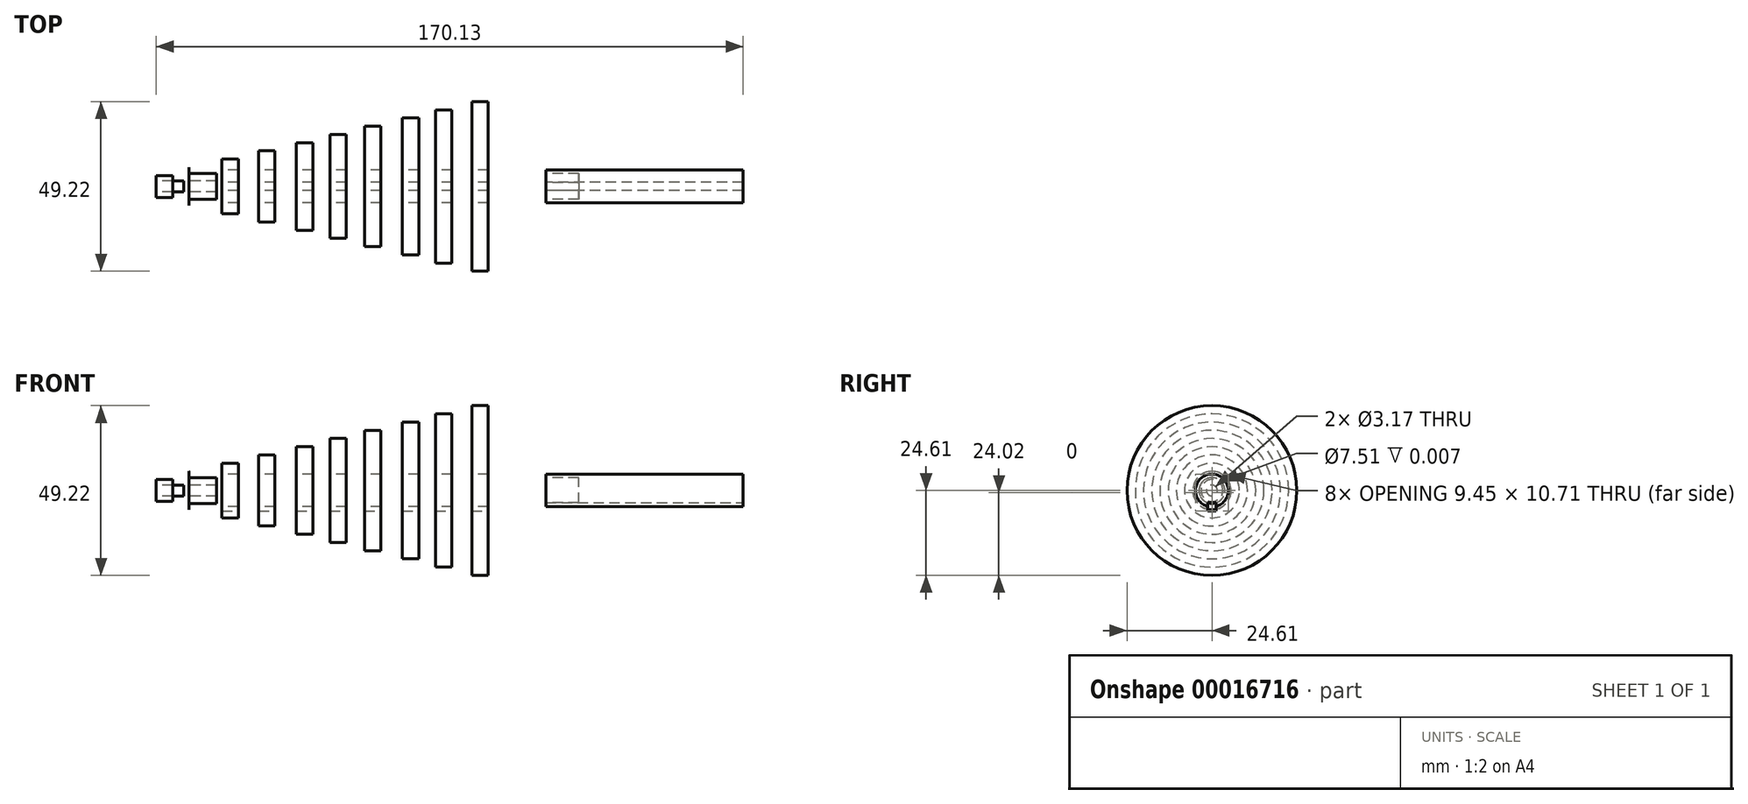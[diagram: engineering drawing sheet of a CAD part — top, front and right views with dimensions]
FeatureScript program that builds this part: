
annotation { "Feature Type Name" : "Feature", "Feature Type Description" : "" }
export const myFeature = defineFeature(function(context is Context, id is Id, definition is map)
    precondition{}
    {
        {
            var Q0;
            Q0=qCreatedBy(makeId("Front.planeOp"),FACE);
            var sketch = newSketch(context, id + "F0", { "sketchPlane" : qUnion([Q0])});
            skLineSegment(sketch, "E0.bottom", {"start": v(-46.34, 7.94) * mm, "end": v(-41.57, 7.94) * mm});
            skLineSegment(sketch, "E0.top", {"start": v(-46.34, 4.76) * mm, "end": v(-41.57, 4.76) * mm});
            skLineSegment(sketch, "E0.left", {"start": v(-46.34, 7.94) * mm, "end": v(-46.34, 4.76) * mm});
            skLineSegment(sketch, "E0.right", {"start": v(-41.57, 7.94) * mm, "end": v(-41.57, 4.76) * mm});
            skLineSegment(sketch, "E1.bottom", {"start": v(-35.72, 10.32) * mm, "end": v(-30.95, 10.32) * mm});
            skLineSegment(sketch, "E1.top", {"start": v(-35.72, 4.76) * mm, "end": v(-30.95, 4.76) * mm});
            skLineSegment(sketch, "E1.left", {"start": v(-35.72, 10.32) * mm, "end": v(-35.72, 4.76) * mm});
            skLineSegment(sketch, "E1.right", {"start": v(-30.95, 10.32) * mm, "end": v(-30.95, 4.76) * mm});
            skLineSegment(sketch, "E2.bottom", {"start": v(-24.77, 12.7) * mm, "end": v(-20.01, 12.7) * mm});
            skLineSegment(sketch, "E2.top", {"start": v(-24.77, 4.76) * mm, "end": v(-20.01, 4.76) * mm});
            skLineSegment(sketch, "E2.left", {"start": v(-24.77, 12.7) * mm, "end": v(-24.77, 4.76) * mm});
            skLineSegment(sketch, "E2.right", {"start": v(-20.01, 12.7) * mm, "end": v(-20.01, 4.76) * mm});
            skLineSegment(sketch, "E3.bottom", {"start": v(-15.05, 15.08) * mm, "end": v(-10.3, 15.08) * mm});
            skLineSegment(sketch, "E3.top", {"start": v(-15.05, 4.76) * mm, "end": v(-10.3, 4.76) * mm});
            skLineSegment(sketch, "E3.left", {"start": v(-15.05, 15.08) * mm, "end": v(-15.05, 4.76) * mm});
            skLineSegment(sketch, "E3.right", {"start": v(-10.3, 15.08) * mm, "end": v(-10.3, 4.76) * mm});
            skLineSegment(sketch, "E4.bottom", {"start": v(-5.01, 17.46) * mm, "end": v(-0.25, 17.46) * mm});
            skLineSegment(sketch, "E4.top", {"start": v(-5.01, 4.76) * mm, "end": v(-0.25, 4.76) * mm});
            skLineSegment(sketch, "E4.left", {"start": v(-5.01, 17.46) * mm, "end": v(-5.01, 4.76) * mm});
            skLineSegment(sketch, "E4.right", {"start": v(-0.25, 17.46) * mm, "end": v(-0.25, 4.76) * mm});
            skLineSegment(sketch, "E5.bottom", {"start": v(6, 19.84) * mm, "end": v(10.76, 19.84) * mm});
            skLineSegment(sketch, "E5.top", {"start": v(6, 4.76) * mm, "end": v(10.76, 4.76) * mm});
            skLineSegment(sketch, "E5.left", {"start": v(6, 19.84) * mm, "end": v(6, 4.76) * mm});
            skLineSegment(sketch, "E5.right", {"start": v(10.76, 19.84) * mm, "end": v(10.76, 4.76) * mm});
            skLineSegment(sketch, "E6.bottom", {"start": v(15.59, 22.23) * mm, "end": v(20.35, 22.23) * mm});
            skLineSegment(sketch, "E6.top", {"start": v(15.59, 4.76) * mm, "end": v(20.35, 4.76) * mm});
            skLineSegment(sketch, "E6.left", {"start": v(15.59, 22.23) * mm, "end": v(15.59, 4.76) * mm});
            skLineSegment(sketch, "E6.right", {"start": v(20.35, 22.23) * mm, "end": v(20.35, 4.76) * mm});
            skLineSegment(sketch, "E7.bottom", {"start": v(26.12, 24.6) * mm, "end": v(30.88, 24.6) * mm});
            skLineSegment(sketch, "E7.top", {"start": v(26.12, 4.76) * mm, "end": v(30.88, 4.76) * mm});
            skLineSegment(sketch, "E7.left", {"start": v(26.12, 24.6) * mm, "end": v(26.12, 4.76) * mm});
            skLineSegment(sketch, "E7.right", {"start": v(30.88, 24.6) * mm, "end": v(30.88, 4.76) * mm});
            skLineSegment(sketch, "E8", {"start": v(-59.84, 0) * mm, "end": v(38.03, 0) * mm, "construction": true});
            skLineSegment(sketch, "E9", {"start": v(-59.07, 4.76) * mm, "end": v(37.83, 4.76) * mm, "construction": true});
            skLineSegment(sketch, "E10.MirrorCS", {"start": v(15.59, -22.23) * mm, "end": v(20.35, -22.23) * mm});
            skLineSegment(sketch, "E11.MirrorCS", {"start": v(-24.77, -12.7) * mm, "end": v(-20.01, -12.7) * mm});
            skLineSegment(sketch, "E12.MirrorCS", {"start": v(-15.05, -15.08) * mm, "end": v(-10.3, -15.08) * mm});
            skLineSegment(sketch, "E13.MirrorCS", {"start": v(15.59, -22.23) * mm, "end": v(15.59, -4.76) * mm});
            skLineSegment(sketch, "E14.MirrorCS", {"start": v(-5.01, -17.46) * mm, "end": v(-5.01, -4.76) * mm});
            skLineSegment(sketch, "E15.MirrorCS", {"start": v(-20.01, -12.7) * mm, "end": v(-20.01, -4.76) * mm});
            skLineSegment(sketch, "E16.MirrorCS", {"start": v(20.35, -22.23) * mm, "end": v(20.35, -4.76) * mm});
            skLineSegment(sketch, "E17.MirrorCS", {"start": v(-35.72, -4.76) * mm, "end": v(-30.95, -4.76) * mm});
            skLineSegment(sketch, "E18.MirrorCS", {"start": v(-35.72, -10.32) * mm, "end": v(-35.72, -4.76) * mm});
            skLineSegment(sketch, "E19.MirrorCS", {"start": v(-24.77, -12.7) * mm, "end": v(-24.77, -4.76) * mm});
            skLineSegment(sketch, "E20.MirrorCS", {"start": v(10.76, -19.84) * mm, "end": v(10.76, -4.76) * mm});
            skLineSegment(sketch, "E21.MirrorCS", {"start": v(26.12, -24.6) * mm, "end": v(26.12, -4.76) * mm});
            skLineSegment(sketch, "E22.MirrorCS", {"start": v(-15.05, -15.08) * mm, "end": v(-15.05, -4.76) * mm});
            skLineSegment(sketch, "E23.MirrorCS", {"start": v(-5.01, -4.76) * mm, "end": v(-0.25, -4.76) * mm});
            skLineSegment(sketch, "E24.MirrorCS", {"start": v(-59.07, -4.76) * mm, "end": v(37.83, -4.76) * mm});
            skLineSegment(sketch, "E25.MirrorCS", {"start": v(-30.95, -10.32) * mm, "end": v(-30.95, -4.76) * mm});
            skLineSegment(sketch, "E26.MirrorCS", {"start": v(6, -19.84) * mm, "end": v(10.76, -19.84) * mm});
            skLineSegment(sketch, "E27.MirrorCS", {"start": v(-5.01, -17.46) * mm, "end": v(-0.25, -17.46) * mm});
            skLineSegment(sketch, "E28.MirrorCS", {"start": v(26.12, -24.6) * mm, "end": v(30.88, -24.6) * mm});
            skLineSegment(sketch, "E29.MirrorCS", {"start": v(6, -4.76) * mm, "end": v(10.76, -4.76) * mm});
            skLineSegment(sketch, "E30.MirrorCS", {"start": v(-15.05, -4.76) * mm, "end": v(-10.3, -4.76) * mm});
            skLineSegment(sketch, "E31.MirrorCS", {"start": v(6, -19.84) * mm, "end": v(6, -4.76) * mm});
            skLineSegment(sketch, "E32.MirrorCS", {"start": v(26.12, -4.76) * mm, "end": v(30.88, -4.76) * mm});
            skLineSegment(sketch, "E33.MirrorCS", {"start": v(15.59, -4.76) * mm, "end": v(20.35, -4.76) * mm});
            skLineSegment(sketch, "E34.MirrorCS", {"start": v(30.88, -24.6) * mm, "end": v(30.88, -4.76) * mm});
            skLineSegment(sketch, "E35.MirrorCS", {"start": v(-10.3, -15.08) * mm, "end": v(-10.3, -4.76) * mm});
            skLineSegment(sketch, "E36.MirrorCS", {"start": v(-0.25, -17.46) * mm, "end": v(-0.25, -4.76) * mm});
            skLineSegment(sketch, "E37.MirrorCS", {"start": v(-35.72, -10.32) * mm, "end": v(-30.95, -10.32) * mm});
            skLineSegment(sketch, "E38.MirrorCS", {"start": v(-46.34, -4.76) * mm, "end": v(-41.57, -4.76) * mm});
            skLineSegment(sketch, "E39.MirrorCS", {"start": v(-46.34, -7.94) * mm, "end": v(-41.57, -7.94) * mm});
            skLineSegment(sketch, "E40.MirrorCS", {"start": v(-41.57, -7.94) * mm, "end": v(-41.57, -4.76) * mm});
            skLineSegment(sketch, "E41.MirrorCS", {"start": v(-46.34, -7.94) * mm, "end": v(-46.34, -4.76) * mm});
            skLineSegment(sketch, "E42.MirrorCS", {"start": v(-24.77, -4.76) * mm, "end": v(-20.01, -4.76) * mm});
            skSolve(sketch);
        }
        {
            var Q0;
            Q0=makeQuery(id+"F0.imprint","IMPRINT",FACE,{"disambiguationData":[TD([[makeQuery(id+"F0.imprint","IMPRINT",EDGE,{"derivedFrom":sQuery(id+"F0.wireOp",EDGE,"E3.bottom")}),-1.0]])]});
            var Q1;
            Q1=makeQuery(id+"F0.imprint","IMPRINT",FACE,{"disambiguationData":[TD([[makeQuery(id+"F0.imprint","IMPRINT",EDGE,{"derivedFrom":sQuery(id+"F0.wireOp",EDGE,"E2.bottom")}),-1.0]])]});
            var Q2;
            Q2=makeQuery(id+"F0.imprint","IMPRINT",FACE,{"disambiguationData":[TD([[makeQuery(id+"F0.imprint","IMPRINT",EDGE,{"derivedFrom":sQuery(id+"F0.wireOp",EDGE,"E1.bottom")}),-1.0]])]});
            var Q3;
            Q3=makeQuery(id+"F0.imprint","IMPRINT",FACE,{"disambiguationData":[TD([[makeQuery(id+"F0.imprint","IMPRINT",EDGE,{"derivedFrom":sQuery(id+"F0.wireOp",EDGE,"E4.bottom")}),-1.0]])]});
            var Q4;
            Q4=makeQuery(id+"F0.imprint","IMPRINT",FACE,{"disambiguationData":[TD([[makeQuery(id+"F0.imprint","IMPRINT",EDGE,{"derivedFrom":sQuery(id+"F0.wireOp",EDGE,"E0.bottom")}),-1.0]])]});
            var Q5;
            Q5=makeQuery(id+"F0.imprint","IMPRINT",FACE,{"disambiguationData":[TD([[makeQuery(id+"F0.imprint","IMPRINT",EDGE,{"derivedFrom":sQuery(id+"F0.wireOp",EDGE,"E5.bottom")}),-1.0]])]});
            var Q6;
            Q6=makeQuery(id+"F0.imprint","IMPRINT",FACE,{"disambiguationData":[TD([[makeQuery(id+"F0.imprint","IMPRINT",EDGE,{"derivedFrom":sQuery(id+"F0.wireOp",EDGE,"E6.bottom")}),-1.0]])]});
            var Q7;
            Q7=makeQuery(id+"F0.imprint","IMPRINT",FACE,{"disambiguationData":[TD([[makeQuery(id+"F0.imprint","IMPRINT",EDGE,{"derivedFrom":sQuery(id+"F0.wireOp",EDGE,"E7.bottom")}),-1.0]])]});
            var Q8;
            Q8=sQuery(id+"F0.wireOp",EDGE,"E8");
            revolve(context, id + "F1", {"entities" : qUnion([Q0, Q1, Q2, Q3, Q4, Q5, Q6, Q7]), "axis" : qUnion([Q8]), "revolveType" : RevolveType.FULL});
        }
        {
            var Q0;
            Q0=qCreatedBy(makeId("Front.planeOp"),FACE);
            var sketch = newSketch(context, id + "F2", { "sketchPlane" : qUnion([Q0])});
            skLineSegment(sketch, "E43.bottom", {"start": v(47.59, 4.76) * mm, "end": v(104.74, 4.76) * mm});
            skLineSegment(sketch, "E43.top", {"start": v(47.59, 0) * mm, "end": v(104.74, 0) * mm});
            skLineSegment(sketch, "E43.left", {"start": v(47.59, 4.76) * mm, "end": v(47.59, 0) * mm});
            skLineSegment(sketch, "E43.right", {"start": v(104.74, 4.76) * mm, "end": v(104.74, 0) * mm});
            skSolve(sketch);
        }
        {
            var Q0;
            Q0 = qSketchRegion(id + "F2", true);
            var Q1;
            Q1=sQuery(id+"F2.wireOp",EDGE,"E43.top");
            revolve(context, id + "F3", {"entities" : qUnion([Q0]), "axis" : qUnion([Q1]), "revolveType" : RevolveType.FULL});
        }
        {
            var Q0;
            Q0=makeQuery(id+"F3.opRevolve","SWEPT_FACE",FACE,{"disambiguationData":[OSD([sQuery(id+"F2.wireOp",EDGE,"E43.left")])]});
            var sketch = newSketch(context, id + "F4", { "sketchPlane" : qUnion([Q0])});
            skCircle(sketch, "E44", {"center": v(0, 0) * mm, "radius": 3.76 * mm});
            skSolve(sketch);
        }
        {
            var Q0;
            Q0 = qSketchRegion(id + "F4", true);
            extrude(context, id + "F5", {"entities" : qUnion([Q0]), "operationType" : NewBodyOperationType.REMOVE, "oppositeDirection" : true, "depth" : 9.52 * mm});
        }
        {
            var Q0;
            Q0=makeQuery(id+"F1.opRevolve","SWEPT_FACE",FACE,{"disambiguationData":[OSD([sQuery(id+"F0.wireOp",EDGE,"E7.right")])]});
            var sketch = newSketch(context, id + "F6", { "sketchPlane" : qUnion([Q0])});
            skLineSegment(sketch, "E45.bottom", {"start": v(-1.18, -3.58) * mm, "end": v(1.18, -3.58) * mm});
            skLineSegment(sketch, "E45.top", {"start": v(-1.18, -5.94) * mm, "end": v(1.18, -5.94) * mm});
            skLineSegment(sketch, "E45.left", {"start": v(-1.18, -3.58) * mm, "end": v(-1.18, -5.94) * mm});
            skLineSegment(sketch, "E45.right", {"start": v(1.18, -3.58) * mm, "end": v(1.18, -5.94) * mm});
            skLineSegment(sketch, "E46", {"start": v(-1.18, -4.76) * mm, "end": v(1.18, -4.76) * mm, "construction": true});
            skLineSegment(sketch, "E47", {"start": v(0, -3.58) * mm, "end": v(0, -5.94) * mm, "construction": true});
            skPoint(sketch, "E48", {"position": v(0, -4.76) * mm});
            skSolve(sketch);
        }
        {
            var Q0;
            {var subQ5=sQuery(id+"F6.wireOp",EDGE,"E45.top");Q0=makeQuery(id+"F6.imprint","IMPRINT",FACE,{"disambiguationData":[TD([[makeQuery(id+"F6.imprint","IMPRINT",EDGE,{"derivedFrom":subQ5}),1.0]])]});}
            var Q1;
            {var subQ5=sQuery(id+"F6.wireOp",EDGE,"E45.bottom");Q1=makeQuery(id+"F6.imprint","IMPRINT",FACE,{"disambiguationData":[TD([[makeQuery(id+"F6.imprint","IMPRINT",EDGE,{"derivedFrom":subQ5}),-1.0]])]});}
            extrude(context, id + "F7", {"entities" : qUnion([Q0, Q1]), "operationType" : NewBodyOperationType.REMOVE, "endBound" : BoundingType.THROUGH_ALL, "oppositeDirection" : true, "depth" : 25.4 * mm, "hasSecondDirection" : true, "secondDirectionBound" : SecondDirectionBoundingType.THROUGH_ALL, "secondDirectionOppositeDirection" : false, "secondDirectionDepth" : 25.4 * mm});
        }
        {
            var Q0;
            Q0=makeQuery(id+"F1.opRevolve","SWEPT_FACE",FACE,{"disambiguationData":[OSD([sQuery(id+"F0.wireOp",EDGE,"E0.left")])]});
            cPlane(context, id + "F8", {"entities" : qUnion([Q0]), "cplaneType" : CPlaneType.OFFSET, "offset" : 9.52 * mm, "width" : 152.4 * mm, "height" : 152.4 * mm});
        }
        {
            var Q0;
            Q0=qCreatedBy(id+"F8.planeOp",FACE);
            var sketch = newSketch(context, id + "F9", { "sketchPlane" : qUnion([Q0])});
            skCircle(sketch, "E49", {"center": v(0, 0) * mm, "radius": 3.75 * mm});
            skCircle(sketch, "E50", {"center": v(0, 0) * mm, "radius": 5.56 * mm});
            skCircle(sketch, "E51", {"center": v(0, 0) * mm, "radius": 1.59 * mm});
            skSolve(sketch);
        }
        {
            var Q0;
            Q0=makeQuery(id+"F9.imprint","IMPRINT",FACE,{"disambiguationData":[TD([[makeQuery(id+"F9.imprint","IMPRINT",EDGE,{"derivedFrom":sQuery(id+"F9.wireOp",EDGE,"E49")}),1.0]])]});
            extrude(context, id + "F10", {"entities" : qUnion([Q0]), "oppositeDirection" : true, "depth" : 7.94 * mm});
        }
        {
            var Q0;
            Q0 = qSketchRegion(id + "F9", true);
            extrude(context, id + "F11", {"entities" : qUnion([Q0]), "oppositeDirection" : true, "depth" : 3 / 406.4 * mm});
        }
        {
            var Q0;
            Q0=makeQuery(id+"F10.opExtrude","CAP_FACE",FACE,{"disambiguationData":[OSD([sQuery(id+"F9.wireOp",EDGE,"E49"),sQuery(id+"F9.wireOp",EDGE,"E51")])],"isStart":true});
            cPlane(context, id + "F12", {"entities" : qUnion([Q0]), "cplaneType" : CPlaneType.OFFSET, "offset" : 9.52 * mm, "width" : 152.4 * mm, "height" : 152.4 * mm});
        }
        {
            var Q0;
            Q0=qCreatedBy(id+"F12.planeOp",FACE);
            var sketch = newSketch(context, id + "F13", { "sketchPlane" : qUnion([Q0])});
            skCircle(sketch, "E52", {"center": v(0, 0) * mm, "radius": 1.59 * mm});
            skCircle(sketch, "E53", {"center": v(0, 0) * mm, "radius": 3.18 * mm});
            skSolve(sketch);
        }
        {
            var Q0;
            Q0=makeQuery(id+"F13.imprint","IMPRINT",FACE,{"disambiguationData":[TD([[makeQuery(id+"F13.imprint","IMPRINT",EDGE,{"derivedFrom":sQuery(id+"F13.wireOp",EDGE,"E52")}),1.0]])]});
            extrude(context, id + "F14", {"entities" : qUnion([Q0]), "oppositeDirection" : true, "depth" : 7.94 * mm});
        }
        {
            var Q0;
            Q0 = qSketchRegion(id + "F13", true);
            extrude(context, id + "F15", {"entities" : qUnion([Q0]), "oppositeDirection" : true, "depth" : 4.76 * mm});
        }
    });
